# Revit family: UCV
name_source: partatom
category: Mechanical Equipment
units: mm (PartAtom-declared; Revit-internal decimal feet)

## family parameters
Always vertical = Yes
Cut with Voids When Loaded = No
Part Type = Normal
Room Calculation Point = No
Round Connector Dimension = Use Diameter
Shared = No
Work Plane-Based = No

## types (10) — shared parameters
0 = 0' - 0"
1" = 0' - 1"
1.5 = 0' - 1 1/2"
2" = 0' - 2"
2' = 2' - 0"
3" = 0' - 3"
4" = 0' - 4"
Manufacturer = Loren Cook Company
Model = UCV
ONE EIGTH = 0' - 0 1/8"
Type Comments = Upblast Centri-Vane All Aluminum Inline Centrifugal Blower Roof Mounted/Belt Drive
URL = www.lorencook.com

## per-type parameters (varying)
- 10_UCV: (D+1")/2=0' - 9 3/32"; (SIZE/2)*.66=0' - 3 5/16"; (T_SQ/2)+.125"=0' - 10 1/8"; (WB_E)/2=0' - 7"; A=1' - 11 1/2"; A/2=0' - 11 3/4"; B=0' - 4 5/8"; B/2=0' - 2 5/16"; C=1' - 3 1/2"; C-2"=1' - 1 1/2"; C/2=0' - 7 3/4"; D=1' - 4 3/16"; D/2=0' - 8 3/32"; E=1' - 3"; E/2=0' - 7 1/2"; F=1' - 6 1/8"; F/2=0' - 9 1/16"; G=0' - 2"; G+(C/2)=0' - 8 3/4"; G+2.5"=0' - 2 1/2"; G-.125"=0' - 1 7/8"; RO=1' - 3 1/2"; RO/2=0' - 7 3/4"; SIZE=0' - 10"; SIZE/2=0' - 5"; T_SQ=1' - 8"; T_SQ/2=0' - 10"; WB_B=0' - 8"; WB_E=1' - 2"
- 12_UCV: (D+1")/2=0' - 10 9/16"; (SIZE/2)*.66=0' - 3 31/32"; (T_SQ/2)+.125"=0' - 10 1/8"; (WB_E)/2=0' - 8"; A=2' - 1 1/8"; A/2=1' - 0 9/16"; B=0' - 5"; B/2=0' - 2 1/2"; C=1' - 5 1/8"; C-2"=1' - 3 1/8"; C/2=0' - 8 9/16"; D=1' - 7 1/8"; D/2=0' - 9 9/16"; E=1' - 3"; E/2=0' - 7 1/2"; F=2' - 3 15/16"; F/2=1' - 1 31/32"; G=0' - 2"; G+(C/2)=0' - 9 9/16"; G+2.5"=0' - 4 1/2"; G-.125"=0' - 1 7/8"; RO=1' - 3 1/2"; RO/2=0' - 7 3/4"; SIZE=1' - 0"; SIZE/2=0' - 6"; T_SQ=1' - 8"; T_SQ/2=0' - 10"; WB_B=0' - 9"; WB_E=1' - 4"
- 14_UCV: (D+1")/2=1' - 0"; (SIZE/2)*.66=0' - 4 5/8"; (T_SQ/2)+.125"=1' - 0 1/8"; (WB_E)/2=0' - 9"; A=2' - 5 1/8"; A/2=1' - 2 9/16"; B=0' - 5"; B/2=0' - 2 1/2"; C=1' - 7 1/8"; C-2"=1' - 5 1/8"; C/2=0' - 9 9/16"; D=1' - 10"; D/2=0' - 11"; E=1' - 4"; E/2=0' - 8"; F=2' - 3 15/16"; F/2=1' - 1 31/32"; G=0' - 2"; G+(C/2)=0' - 10 9/16"; G+2.5"=0' - 4 1/2"; G-.125"=0' - 1 7/8"; RO=1' - 7 1/2"; RO/2=0' - 9 3/4"; SIZE=1' - 2"; SIZE/2=0' - 7"; T_SQ=2' - 0"; T_SQ/2=1' - 0"; WB_B=0' - 10"; WB_E=1' - 6"
- 16_UCV: (D+1")/2=1' - 1 7/16"; (SIZE/2)*.66=0' - 5 9/32"; (T_SQ/2)+.125"=1' - 0 1/8"; (WB_E)/2=0' - 10 1/2"; A=2' - 7 9/16"; A/2=1' - 3 25/32"; B=0' - 5"; B/2=0' - 2 1/2"; C=1' - 9 9/16"; C-2"=1' - 7 9/16"; C/2=0' - 10 25/32"; D=2' - 0 7/8"; D/2=1' - 0 7/16"; E=1' - 5"; E/2=0' - 8 1/2"; F=2' - 3 15/16"; F/2=1' - 1 31/32"; G=0' - 2"; G+(C/2)=0' - 11 25/32"; G+2.5"=0' - 4 1/2"; G-.125"=0' - 1 7/8"; RO=1' - 7 1/2"; RO/2=0' - 9 3/4"; SIZE=1' - 4"; SIZE/2=0' - 8"; T_SQ=2' - 0"; T_SQ/2=1' - 0"; WB_B=0' - 11"; WB_E=1' - 9"
- 18_UCV: (D+1")/2=1' - 2 7/8"; (SIZE/2)*.66=0' - 5 15/16"; (T_SQ/2)+.125"=1' - 2 1/8"; (WB_E)/2=0' - 11 1/2"; A=3' - 0 1/2"; A/2=1' - 6 1/4"; B=0' - 5"; B/2=0' - 2 1/2"; C=2' - 0 1/2"; C-2"=1' - 10 1/2"; C/2=1' - 0 1/4"; D=2' - 3 3/4"; D/2=1' - 1 7/8"; E=1' - 7"; E/2=0' - 9 1/2"; F=2' - 3 15/16"; F/2=1' - 1 31/32"; G=0' - 2"; G+(C/2)=1' - 1 1/4"; G+2.5"=0' - 4 1/2"; G-.125"=0' - 1 7/8"; RO=1' - 11 1/2"; RO/2=0' - 11 3/4"; SIZE=1' - 6"; SIZE/2=0' - 9"; T_SQ=2' - 4"; T_SQ/2=1' - 2"; WB_B=1' - 0"; WB_E=1' - 11"
- 20_UCV: (D+1")/2=1' - 4 1/4"; (SIZE/2)*.66=0' - 6 19/32"; (T_SQ/2)+.125"=1' - 2 1/8"; (WB_E)/2=1' - 0 1/2"; A=3' - 2 1/2"; A/2=1' - 7 1/4"; B=0' - 6 3/4"; B/2=0' - 3 3/8"; C=2' - 2 1/2"; C-2"=2' - 0 1/2"; C/2=1' - 1 1/4"; D=2' - 6 1/2"; D/2=1' - 3 1/4"; E=1' - 7"; E/2=0' - 9 1/2"; F=3' - 0"; F/2=1' - 6"; G=0' - 2"; G+(C/2)=1' - 2 1/4"; G+2.5"=0' - 4 1/2"; G-.125"=0' - 1 7/8"; RO=1' - 11 1/2"; RO/2=0' - 11 3/4"; SIZE=1' - 8"; SIZE/2=0' - 10"; T_SQ=2' - 4"; T_SQ/2=1' - 2"; WB_B=1' - 1"; WB_E=2' - 1"
- 24_UCV: (D+1")/2=1' - 7 1/4"; (SIZE/2)*.66=0' - 7 29/32"; (T_SQ/2)+.125"=1' - 4 1/8"; (WB_E)/2=1' - 2 1/2"; A=3' - 9 3/8"; A/2=1' - 10 11/16"; B=0' - 6 3/4"; B/2=0' - 3 3/8"; C=2' - 7 3/8"; C-2"=2' - 5 3/8"; C/2=1' - 3 11/16"; D=3' - 0 1/2"; D/2=1' - 6 1/4"; E=1' - 9"; E/2=0' - 10 1/2"; F=3' - 0"; F/2=1' - 6"; G=0' - 3"; G+(C/2)=1' - 5 11/16"; G+2.5"=0' - 5 1/2"; G-.125"=0' - 2 7/8"; RO=2' - 3 1/2"; RO/2=1' - 1 3/4"; SIZE=2' - 0"; SIZE/2=1' - 0"; T_SQ=2' - 8"; T_SQ/2=1' - 4"; WB_B=1' - 3"; WB_E=2' - 5"
- 28_UCV: (D+1")/2=1' - 10"; (SIZE/2)*.66=0' - 9 1/4"; (T_SQ/2)+.125"=1' - 6 1/8"; (WB_E)/2=1' - 4 1/2"; A=4' - 4"; A/2=2' - 2"; B=0' - 8"; B/2=0' - 4"; C=3' - 0"; C-2"=2' - 10"; C/2=1' - 6"; D=3' - 6"; D/2=1' - 9"; E=2' - 5"; E/2=1' - 2 1/2"; F=3' - 6 1/8"; F/2=1' - 9 1/16"; G=0' - 3"; G+(C/2)=1' - 8"; G+2.5"=0' - 5 1/2"; G-.125"=0' - 2 7/8"; RO=2' - 7 1/2"; RO/2=1' - 3 3/4"; SIZE=2' - 4"; SIZE/2=1' - 2"; T_SQ=3' - 0"; T_SQ/2=1' - 6"; WB_B=1' - 5"; WB_E=2' - 9"
- 32_UCV: (D+1")/2=2' - 1"; (SIZE/2)*.66=0' - 10 9/16"; (T_SQ/2)+.125"=1' - 9 1/8"; (WB_E)/2=1' - 6 1/2"; A=4' - 10 7/8"; A/2=2' - 5 7/16"; B=1' - 5"; B/2=0' - 8 1/2"; C=3' - 4 7/8"; C-2"=3' - 2 7/8"; C/2=1' - 8 7/16"; D=4' - 0"; D/2=2' - 0"; E=2' - 6"; E/2=1' - 3"; F=4' - 4"; F/2=2' - 2"; G=0' - 3"; G+(C/2)=1' - 10 7/16"; G+2.5"=0' - 5 1/2"; G-.125"=0' - 2 7/8"; RO=3' - 1 1/2"; RO/2=1' - 6 3/4"; SIZE=2' - 8"; SIZE/2=1' - 4"; T_SQ=3' - 6"; T_SQ/2=1' - 9"; WB_B=1' - 7"; WB_E=3' - 1"
- 36_UCV: (D+1")/2=2' - 3 11/16"; (SIZE/2)*.66=0' - 10 9/16"; (T_SQ/2)+.125"=2' - 0 1/8"; (WB_E)/2=1' - 8 1/2"; A=5' - 4"; A/2=2' - 8"; B=1' - 5 1/2"; B/2=0' - 8 3/4"; C=3' - 8"; C-2"=3' - 6"; C/2=1' - 10"; D=4' - 5 3/8"; D/2=2' - 2 11/16"; E=2' - 8"; E/2=1' - 4"; F=5' - 2"; F/2=2' - 7"; G=0' - 3"; G+(C/2)=2' - 0"; G+2.5"=0' - 5 1/2"; G-.125"=0' - 2 7/8"; RO=3' - 7 1/2"; RO/2=1' - 9 3/4"; SIZE=2' - 8"; SIZE/2=1' - 4"; T_SQ=4' - 0"; T_SQ/2=2' - 0"; WB_B=1' - 9"; WB_E=3' - 5"

## geometry (parser evidence)
native form markers: Sweep x2
no freeform markers — native parametric forms only
